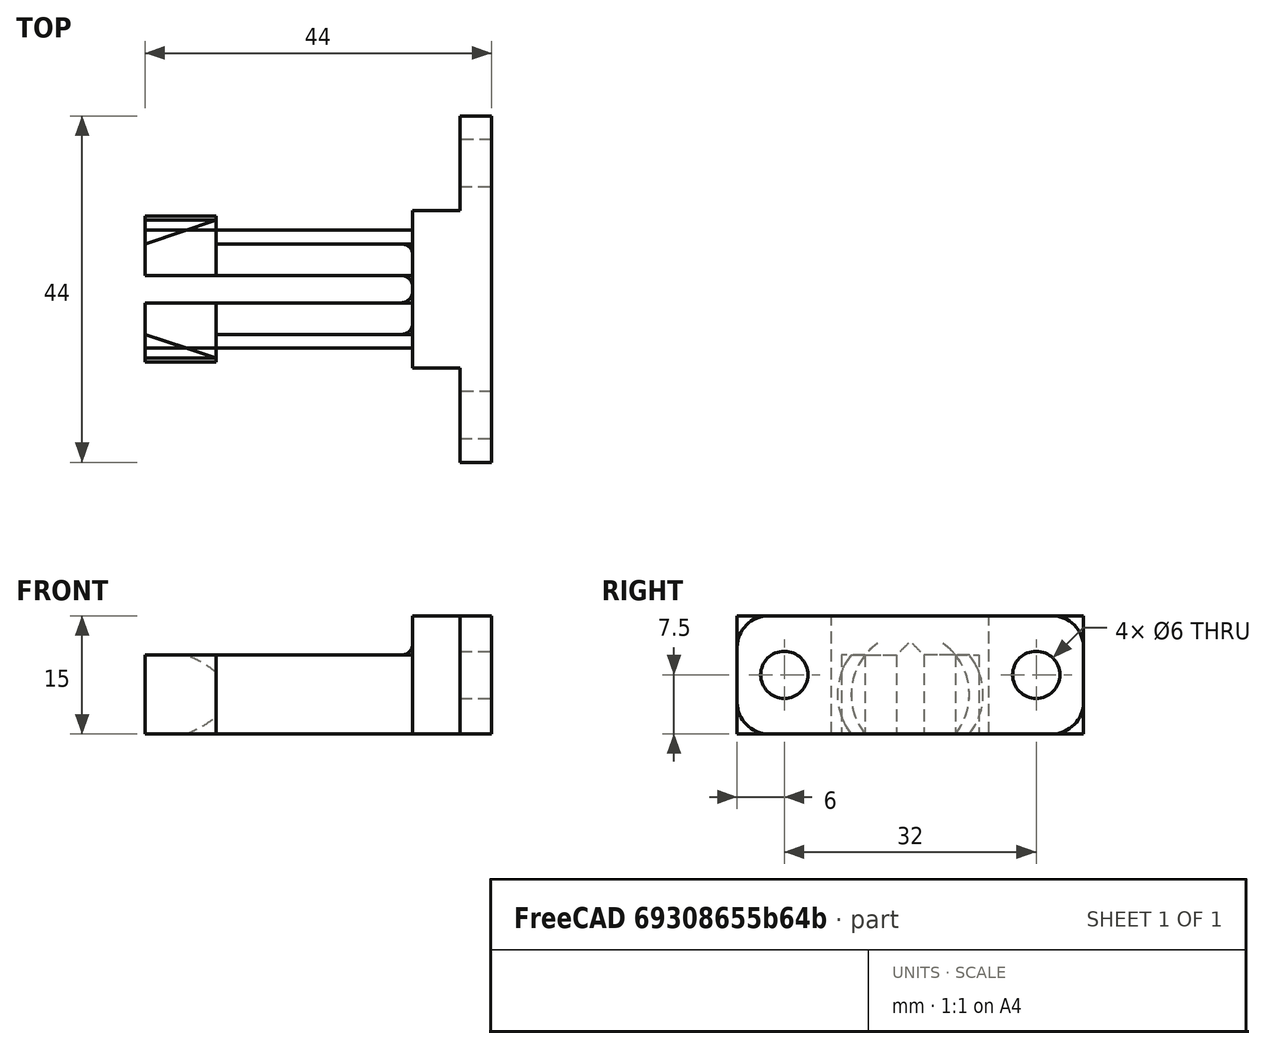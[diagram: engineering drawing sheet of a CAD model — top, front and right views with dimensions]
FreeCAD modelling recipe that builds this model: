
FCSTD DOCUMENT  (FreeCAD 0.14R2756 (Git))
Label: feed_tube_holder_v2.0
License: CC-BY 3.0
LicenseURL: http://creativecommons.org/licenses/by/3.0/
objects: Sketcher::SketchObject×5, PartDesign::Pad×3, PartDesign::Pocket×2, PartDesign::Fillet×2, Part::Feature×1, Mesh::Feature×1
note: 18 computed .brp shape members not serialized (recipe doc carries the construction recipe); baked Part::Feature solids carry a one-line shape summary decoded from their .brp

FEATURE [Sketcher::SketchObject] Sketch
  sketch-geometry (8):
    g0: LineSegment StartX=0 StartY=0 StartZ=0 EndX=-4 EndY=0 EndZ=0
    g1: LineSegment StartX=-4 StartY=0 StartZ=0 EndX=-4 EndY=12 EndZ=0
    g2: LineSegment StartX=-4 StartY=12 StartZ=0 EndX=-10 EndY=12 EndZ=0
    g3: LineSegment StartX=-10 StartY=12 StartZ=0 EndX=-10 EndY=32 EndZ=0
    g4: LineSegment StartX=-10 StartY=32 StartZ=0 EndX=-4 EndY=32 EndZ=0
    g5: LineSegment StartX=-4 StartY=32 StartZ=0 EndX=-4 EndY=44 EndZ=0
    g6: LineSegment StartX=-4 StartY=44 StartZ=0 EndX=0 EndY=44 EndZ=0
    g7: LineSegment StartX=0 StartY=44 StartZ=0 EndX=0 EndY=0 EndZ=0
  constraints (23):
    c: PointOnObject(g0,g-1)
    c: Coincident(g0,g1)
    c: Vertical(g1)
    c: Coincident(g1,g2)
    c: Vertical(g3)
    c: Coincident(g3,g4)
    c: Coincident(g4,g5)
    c: Vertical(g5)
    c: Coincident(g5,g6)
    c: Horizontal(g6)
    c: Coincident(g6,g7)
    c: Coincident(g7,g-1)
    c: Vertical(g7)
    c: DistanceX(g-1,g0) = -4
    c: Equal(g6,g0)
    c: Equal(g1,g5)
    c: Coincident(g-1,g0)
    c: Horizontal(g4)
    c: DistanceY(g1,g0) = -12
    c: Coincident(g2,g3)
    c: Horizontal(g2)
    c: DistanceX(g1,g2) = -6
    c: DistanceY(g2,g3) = 20
FEATURE [PartDesign::Pad] Pad
  Length = 15
  Length2 = 100
  Sketch = -> Sketch
  Type = 0
FEATURE [Sketcher::SketchObject] Sketch001
  Placement = pos=(-10,0,0) rot=(0.57735,-0.57735,-0.57735;2.0944rad)
  Support = -> Pad [Face4]
  sketch-geometry (8):
    g0: LineSegment StartX=-27.75 StartY=10 StartZ=0 EndX=-23.75 EndY=10 EndZ=0
    g1: LineSegment StartX=-23.75 StartY=10 StartZ=0 EndX=-23.75 EndY=0 EndZ=0
    g2: LineSegment StartX=-23.75 StartY=0 StartZ=0 EndX=-27.75 EndY=0 EndZ=0
    g3: LineSegment StartX=-16.25 StartY=10 StartZ=0 EndX=-20.25 EndY=10 EndZ=0
    g4: LineSegment StartX=-20.25 StartY=10 StartZ=0 EndX=-20.25 EndY=0 EndZ=0
    g5: LineSegment StartX=-20.25 StartY=0 StartZ=0 EndX=-16.25 EndY=0 EndZ=0
    g6: ArcOfCircle CenterX=-21.505 CenterY=5 CenterZ=0 NormalX=0 NormalY=0 NormalZ=1 Radius=8 StartAngle=2.46646 EndAngle=3.81672
    g7: ArcOfCircle CenterX=-22.495 CenterY=5 CenterZ=0 NormalX=0 NormalY=0 NormalZ=1 Radius=8 StartAngle=5.60805 EndAngle=6.95832
  constraints (26):
    c: Horizontal(g0)
    c: Coincident(g0,g1)
    c: Vertical(g1)
    c: Coincident(g1,g2)
    c: Horizontal(g2)
    c: Coincident(g3,g4)
    c: Vertical(g4)
    c: Coincident(g4,g5)
    c: Horizontal(g5)
    c: Equal(g5,g2)
    c: Equal(g2,g0)
    c: Equal(g0,g3)
    c: Horizontal(g3)
    c: PointOnObject(g0,g3)
    c: PointOnObject(g1,g5)
    c: DistanceX(g1,g4) = 3.5
    c: DistanceX(g4,g5) = 4
    c: Coincident(g6,g0)
    c: Coincident(g7,g3)
    c: Coincident(g7,g5)
    c: Equal(g7,g6)
    c: Coincident(g6,g2)
    c: Radius(g6) = 8
    c: PointOnObject(g-1,g5)
    c: DistanceY(g4,g3) = 10
    c: DistanceX(g-1,g4) = -20.25
FEATURE [PartDesign::Pad] Pad001
  Length = 25
  Length2 = 100
  Sketch = -> Sketch001
  Type = 0
FEATURE [Sketcher::SketchObject] Sketch002
  ExternalGeometry = -> [Pad001]
  Placement = pos=(-35,0,0) rot=(0.57735,-0.57735,-0.57735;2.0944rad)
  Support = -> Pad001 [Face20]
  sketch-geometry (8):
    g0: LineSegment StartX=-29.5 StartY=10 StartZ=0 EndX=-23.75 EndY=10 EndZ=0
    g1: LineSegment StartX=-23.75 StartY=10 StartZ=0 EndX=-23.75 EndY=0 EndZ=0
    g2: LineSegment StartX=-23.75 StartY=0 StartZ=0 EndX=-29.5 EndY=0 EndZ=0
    g3: LineSegment StartX=-14.5 StartY=10 StartZ=0 EndX=-20.25 EndY=10 EndZ=0
    g4: LineSegment StartX=-20.25 StartY=10 StartZ=0 EndX=-20.25 EndY=0 EndZ=0
    g5: LineSegment StartX=-20.25 StartY=0 StartZ=0 EndX=-14.5 EndY=0 EndZ=0
    g6: ArcOfCircle CenterX=-23.255 CenterY=5 CenterZ=0 NormalX=0 NormalY=0 NormalZ=1 Radius=8 StartAngle=2.46646 EndAngle=3.81672
    g7: ArcOfCircle CenterX=-20.745 CenterY=5 CenterZ=0 NormalX=0 NormalY=0 NormalZ=1 Radius=8 StartAngle=5.60805 EndAngle=6.95832
  constraints (23):
    c: Horizontal(g0)
    c: Coincident(g0,g1)
    c: Coincident(g1,g-3)
    c: Vertical(g1)
    c: Coincident(g1,g2)
    c: Horizontal(g2)
    c: Coincident(g3,g-4)
    c: Horizontal(g3)
    c: Coincident(g3,g4)
    c: Coincident(g4,g-4)
    c: Coincident(g4,g5)
    c: PointOnObject(g5,g-1)
    c: Equal(g5,g2)
    c: Equal(g2,g0)
    c: Equal(g0,g3)
    c: Coincident(g-3,g0)
    c: Coincident(g6,g0)
    c: Coincident(g7,g3)
    c: Coincident(g7,g5)
    c: Equal(g7,g6)
    c: Coincident(g6,g2)
    c: Radius(g6) = 8
    c: DistanceX(g0,g3) = 15
FEATURE [PartDesign::Pad] Pad002
  Length = 9
  Length2 = 100
  Sketch = -> Sketch002
  Type = 0
FEATURE [Sketcher::SketchObject] Sketch003
  ExternalGeometry = -> [Pad002]
  Placement = pos=(0,0,10) rot=(0,0,1;0rad)
  Support = -> Pad002 [Face22]
  sketch-geometry (6):
    g0: LineSegment StartX=-44 StartY=16.25 StartZ=0 EndX=-35 EndY=13.25 EndZ=0
    g1: LineSegment StartX=-35 StartY=13.25 StartZ=0 EndX=-44 EndY=13.25 EndZ=0
    g2: LineSegment StartX=-44 StartY=13.25 StartZ=0 EndX=-44 EndY=16.25 EndZ=0
    g3: LineSegment StartX=-44 StartY=27.75 StartZ=0 EndX=-35 EndY=30.75 EndZ=0
    g4: LineSegment StartX=-35 StartY=30.75 StartZ=0 EndX=-44 EndY=30.75 EndZ=0
    g5: LineSegment StartX=-44 StartY=30.75 StartZ=0 EndX=-44 EndY=27.75 EndZ=0
  constraints (18):
    c: PointOnObject(g0,g-4)
    c: Coincident(g0,g1)
    c: Horizontal(g1)
    c: Coincident(g1,g2)
    c: Coincident(g2,g0)
    c: PointOnObject(g3,g-3)
    c: Coincident(g3,g4)
    c: Horizontal(g4)
    c: Coincident(g4,g5)
    c: Coincident(g5,g3)
    c: PointOnObject(g3,g-5)
    c: PointOnObject(g0,g-5)
    c: DistanceY(g0,g-4) = 4
    c: Vertical(g2)
    c: DistanceY(g1,g0) = 3
    c: Vertical(g5)
    c: Equal(g5,g2)
    c: DistanceY(g-3,g3) = 4
FEATURE [PartDesign::Pocket] Pocket
  Length = 10
  Sketch = -> Sketch003
  Type = 0
FEATURE [Sketcher::SketchObject] Sketch004
  ExternalGeometry = -> [Pocket]
  Placement = pos=(0,0,0) rot=(0.57735,0.57735,0.57735;2.0944rad)
  Support = -> Pocket [Face2]
  sketch-geometry (3):
    g0: Circle CenterX=6 CenterY=7.5 CenterZ=0 NormalX=0 NormalY=0 NormalZ=1 Radius=3
    g1: Circle CenterX=38 CenterY=7.5 CenterZ=0 NormalX=0 NormalY=0 NormalZ=1 Radius=3
    g2: LineSegment [constr] StartX=6 StartY=7.5 StartZ=0 EndX=38 EndY=7.5 EndZ=0
  constraints (8):
    c: Coincident(g2,g0)
    c: Coincident(g2,g1)
    c: Horizontal(g2)
    c: Equal(g1,g0)
    c: Radius(g0) = 3
    c: DistanceX(g-1,g0) = 6
    c: DistanceY(g-1,g0) = 7.5
    c: DistanceX(g-3,g1) = -6
FEATURE [PartDesign::Pocket] Pocket001
  Length = 5
  Sketch = -> Sketch004
  Type = 0
FEATURE [PartDesign::Fillet] Fillet
  Base = -> Pocket001 [Edge3,Edge4,Edge15,Edge28]
  Radius = 4
FEATURE [PartDesign::Fillet] Fillet001
  Base = -> Fillet [Edge52,Edge51,Edge50,Edge53]
  Radius = 1.5
FEATURE [Part::Feature] Fillet001001  label="Fillet002"
  shape: bbox 44 x 44 x 15 mm, 36 faces (baked)
FEATURE [Mesh::Feature] Mesh  label="Fillet002 (Meshed)"
